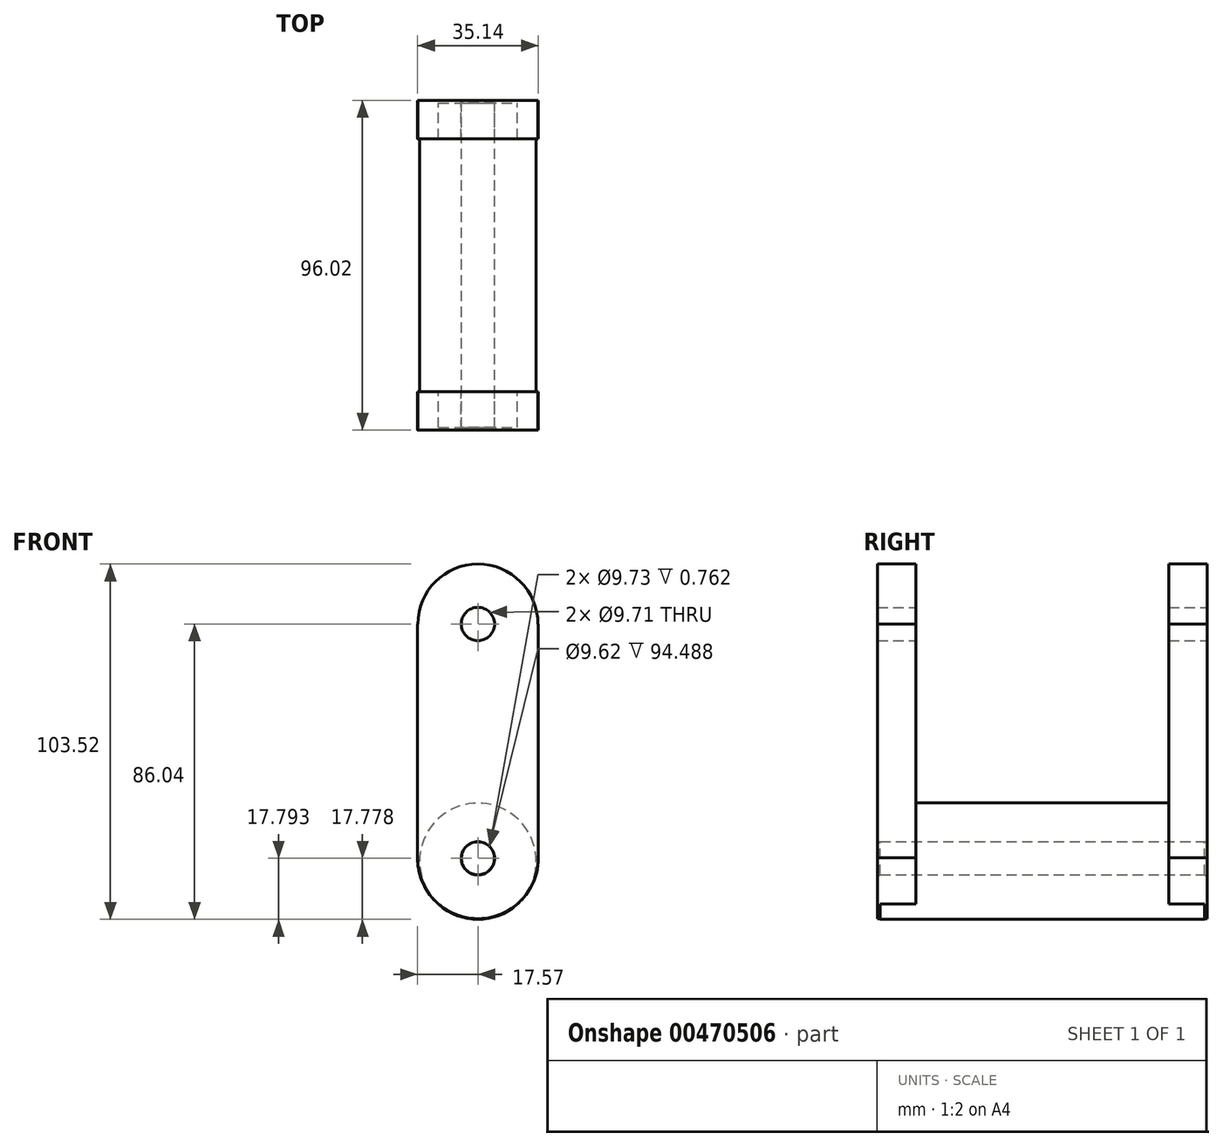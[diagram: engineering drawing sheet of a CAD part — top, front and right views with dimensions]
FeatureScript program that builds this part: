
annotation { "Feature Type Name" : "Feature", "Feature Type Description" : "" }
export const myFeature = defineFeature(function(context is Context, id is Id, definition is map)
    precondition{}
    {
        {
            var Q0;
            Q0=qCreatedBy(makeId("Front.planeOp"),FACE);
            var sketch = newSketch(context, id + "F0", { "sketchPlane" : qUnion([Q0])});
            skArc(sketch, "E0", {"start": v(-17.57, 17.8) * mm, "mid": v(0, 0) * mm, "end": v(17.57, 17.8) * mm});
            skLineSegment(sketch, "E1.top", {"start": v(17.57, 85.83) * mm, "end": v(17.48, 85.83) * mm});
            skLineSegment(sketch, "E1.left", {"start": v(17.57, 17.8) * mm, "end": v(17.57, 85.83) * mm});
            skLineSegment(sketch, "E1.right", {"start": v(-17.57, 17.8) * mm, "end": v(-17.57, 85.83) * mm});
            skPoint(sketch, "E1.middle", {"position": v(0, 51.82) * mm});
            skArc(sketch, "E2", {"start": v(17.48, 85.83) * mm, "mid": v(0, 103.31) * mm, "end": v(-17.48, 85.83) * mm});
            skCircle(sketch, "E3", {"center": v(0, 85.83) * mm, "radius": 4.85 * mm});
            skCircle(sketch, "E4", {"center": v(0, 17.57) * mm, "radius": 4.86 * mm});
            skLineSegment(sketch, "E5.trimOffspring", {"start": v(-17.48, 85.83) * mm, "end": v(-17.57, 85.83) * mm});
            skSolve(sketch);
        }
        {
            var Q0;
            Q0 = qSketchRegion(id + "F0", true);
            extrude(context, id + "F1", {"entities" : qUnion([Q0]), "endBound" : BoundingType.SYMMETRIC, "depth" : 96.01 * mm});
        }
        {
            var Q0;
            Q0 = qSketchRegion(id + "F0", true);
            extrude(context, id + "F2", {"entities" : qUnion([Q0]), "operationType" : NewBodyOperationType.REMOVE, "endBound" : BoundingType.SYMMETRIC, "depth" : 73.66 * mm});
        }
        {
            var Q0;
            Q0=qCreatedBy(makeId("Front.planeOp"),FACE);
            var sketch = newSketch(context, id + "F3", { "sketchPlane" : qUnion([Q0])});
            skCircle(sketch, "E6", {"center": v(0, 16.75) * mm, "radius": 16.96 * mm});
            skCircle(sketch, "E7", {"center": v(0, 17.58) * mm, "radius": 4.8 * mm});
            skSolve(sketch);
        }
        {
            var Q0;
            Q0 = qSketchRegion(id + "F3", true);
            extrude(context, id + "F4", {"entities" : qUnion([Q0]), "operationType" : NewBodyOperationType.ADD, "endBound" : BoundingType.SYMMETRIC, "depth" : 94.49 * mm});
        }
    });
